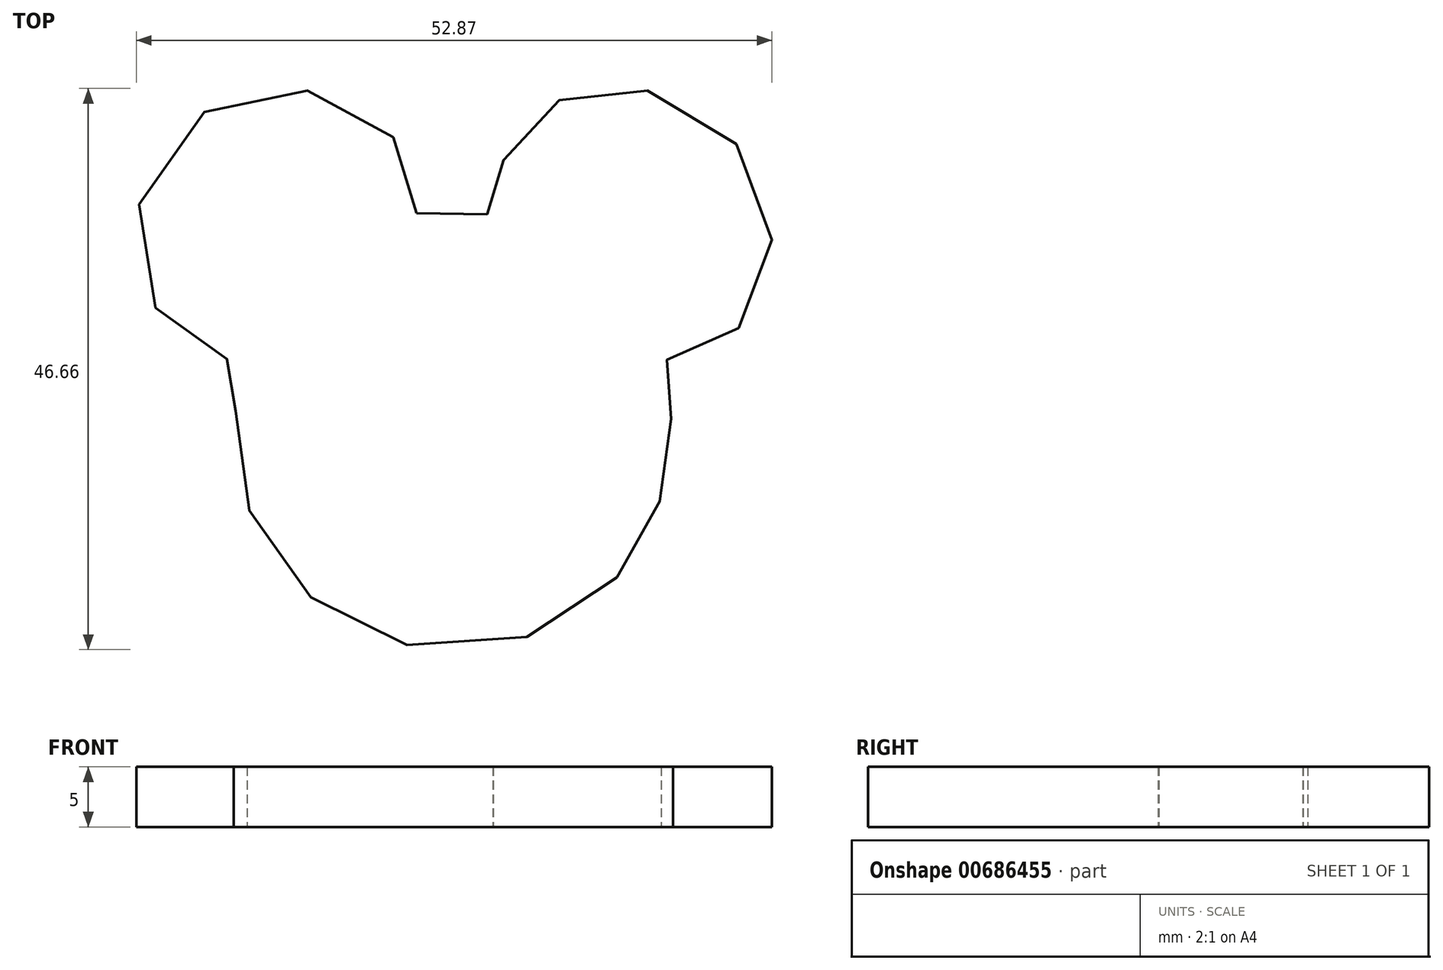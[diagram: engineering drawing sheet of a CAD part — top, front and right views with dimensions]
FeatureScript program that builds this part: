
annotation { "Feature Type Name" : "Feature", "Feature Type Description" : "" }
export const myFeature = defineFeature(function(context is Context, id is Id, definition is map)
    precondition{}
    {
        {
            var Q0;
            Q0=qCreatedBy(makeId("Top.planeOp"),FACE);
            var sketch = newSketch(context, id + "F0", { "sketchPlane" : qUnion([Q0])});
            skFitSpline(sketch, "E0", {"points": [v(-32.26, 38.16) * mm, v(-30.12, 38.37) * mm, v(-27.43, 38.23) * mm, v(-25.98, 38.16) * mm, v(-25.9, 38.92) * mm, v(-25.63, 40.93) * mm, v(-24.6, 43.48) * mm, v(-23.07, 45.7) * mm, v(-19.62, 47.9) * mm, v(-16.1, 48.53) * mm, v(-12.1, 48.18) * mm, v(-7.6, 45.9) * mm, v(-3.94, 41.34) * mm, v(-2.7, 36.78) * mm, v(-3.46, 32.02) * mm, v(-5.4, 28.7) * mm, v(-7.53, 27.04) * mm, v(-10.92, 26) * mm, v(-11.88, 25.8) * mm, v(-11.47, 24.35) * mm, v(-11.12, 21.58) * mm, v(-10.92, 19.17) * mm, v(-11.6, 15.57) * mm, v(-12.92, 11.78) * mm, v(-14.65, 8.94) * mm, v(-17.9, 5.83) * mm, v(-23.07, 2.93) * mm, v(-30.05, 1.9) * mm, v(-36, 3.2) * mm, v(-40.62, 5.9) * mm, v(-43.73, 9.01) * mm, v(-46.63, 14.68) * mm, v(-47.46, 19.44) * mm, v(-46.9, 23.66) * mm, v(-46.42, 26) * mm, v(-47.6, 26) * mm, v(-51.12, 27.32) * mm, v(-53.68, 29.8) * mm, v(-55.4, 34.7) * mm, v(-55.06, 39.9) * mm, v(-51.67, 45.2) * mm, v(-46.5, 48.11) * mm, v(-41.45, 48.39) * mm, v(-36.54, 46.8) * mm, v(-33.78, 43.9) * mm, v(-32.68, 41.06) * mm, v(-32.26, 38.16) * mm]});
            skSolve(sketch);
        }
        {
            var Q0;
            Q0 = qSketchRegion(id + "F0", true);
            extrude(context, id + "F1", {"entities" : qUnion([Q0]), "depth" : 5 * mm, "offsetDistance" : 25 * mm});
        }
    });
